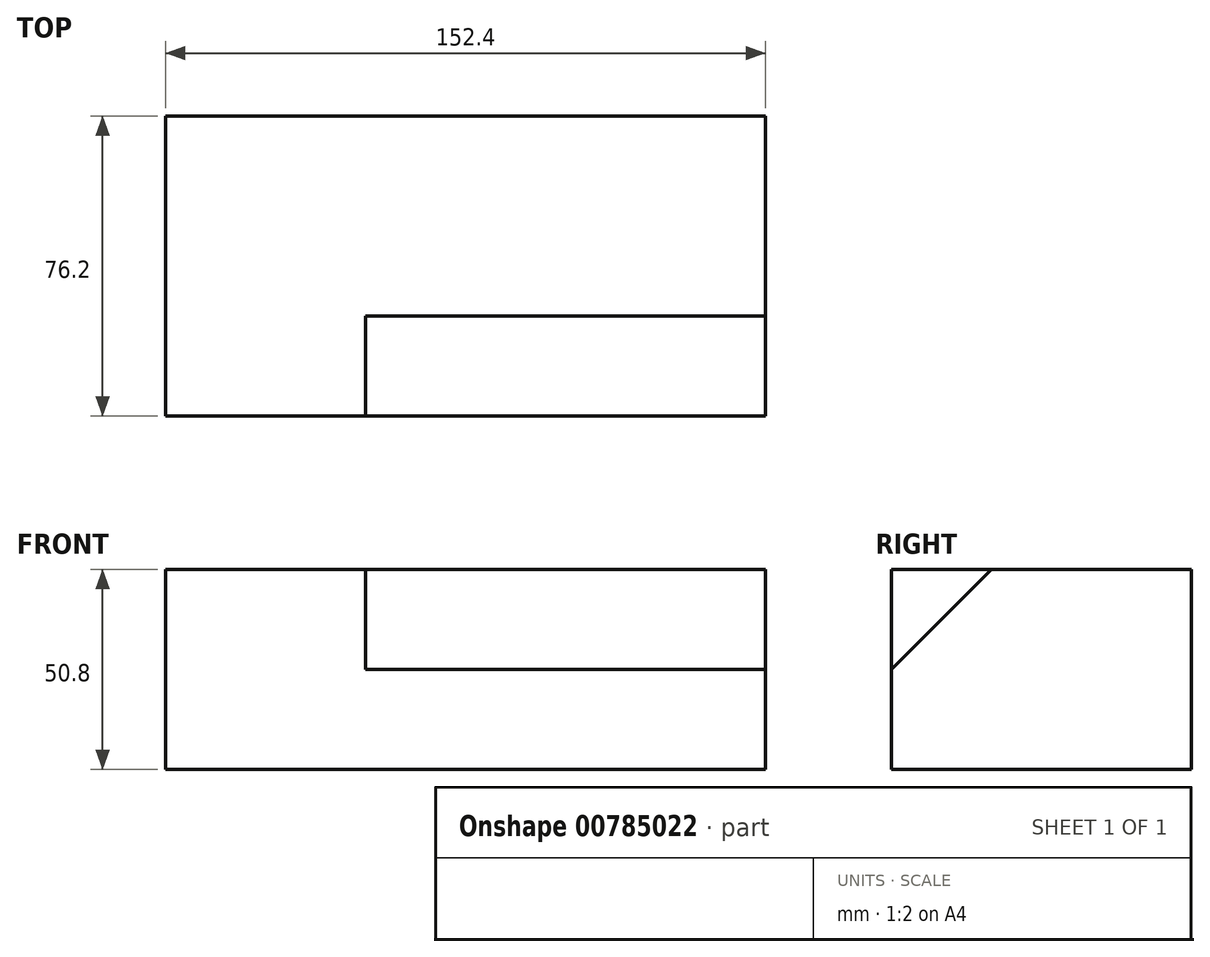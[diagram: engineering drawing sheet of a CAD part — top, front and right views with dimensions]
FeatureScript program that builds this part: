
annotation { "Feature Type Name" : "Feature", "Feature Type Description" : "" }
export const myFeature = defineFeature(function(context is Context, id is Id, definition is map)
    precondition{}
    {
        {
            var Q0;
            Q0=qCreatedBy(makeId("Front.planeOp"),FACE);
            var sketch = newSketch(context, id + "F0", { "sketchPlane" : qUnion([Q0])});
            skLineSegment(sketch, "E0", {"start": v(0, 0) * mm, "end": v(152.4, 0) * mm});
            skLineSegment(sketch, "E1", {"start": v(152.4, 0) * mm, "end": v(152.4, 50.8) * mm});
            skLineSegment(sketch, "E2", {"start": v(152.4, 50.8) * mm, "end": v(0, 50.8) * mm});
            skLineSegment(sketch, "E3", {"start": v(0, 50.8) * mm, "end": v(0, 0) * mm});
            skSolve(sketch);
        }
        {
            var Q0;
            Q0=makeQuery(id+"F0.imprint","IMPRINT",FACE,{"disambiguationData":[TD([[makeQuery(id+"F0.imprint","IMPRINT",EDGE,{"derivedFrom":sQuery(id+"F0.wireOp",EDGE,"E0")}),1.0]])]});
            extrude(context, id + "F1", {"entities" : qUnion([Q0]), "depth" : 76.2 * mm, "offsetDistance" : 25.4 * mm});
        }
        {
            var Q0;
            Q0=makeQuery(id+"F1.opExtrude","SWEPT_FACE",FACE,{"disambiguationData":[OSD([sQuery(id+"F0.wireOp",EDGE,"E1")])]});
            var sketch = newSketch(context, id + "F2", { "sketchPlane" : qUnion([Q0])});
            skLineSegment(sketch, "E4", {"start": v(-76.2, 0) * mm, "end": v(-76.2, 25.4) * mm});
            skLineSegment(sketch, "E5", {"start": v(0, 0) * mm, "end": v(-50.8, 0) * mm});
            skLineSegment(sketch, "E6", {"start": v(-50.8, 0) * mm, "end": v(-50.8, 50.8) * mm});
            skLineSegment(sketch, "E7", {"start": v(-50.8, 50.8) * mm, "end": v(-76.2, 25.4) * mm});
            skSolve(sketch);
        }
        {
            var Q0;
            {var subQ0=sQuery(id+"F2.wireOp",EDGE,"E7");Q0=makeQuery(id+"F2.imprint","IMPRINT",FACE,{"disambiguationData":[TD([[makeQuery(id+"F2.imprint","IMPRINT",EDGE,{"derivedFrom":subQ0}),-1.0]])]});}
            extrude(context, id + "F3", {"entities" : qUnion([Q0]), "operationType" : NewBodyOperationType.REMOVE, "oppositeDirection" : true, "depth" : 101.6 * mm, "offsetDistance" : 25.4 * mm});
        }
    });
